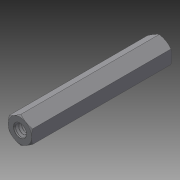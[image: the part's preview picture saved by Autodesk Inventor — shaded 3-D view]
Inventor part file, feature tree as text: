
AUTODESK INVENTOR PART (.ipt)
format: ipt  version: 2015 (Build 190159000, 159)  size: 840,704 bytes
history: native  units: in
note: dims shown in document units (in); Inventor stores cm internally (conversion verified against a paired STEP export)
features: hole x18, sketch x10, other x1, imported_body x1
ambient origin geometry x8: Origin, YZ Plane, XZ Plane, XY Plane, X Axis, Y Axis, Z Axis, Center Point
bodies: Solid1 (feature_tree)
feature tree (30):
  other  "91780A337.sat1"
  hole  "Hole1"  [1 undecoded]
  hole  "Hole2"  [1 undecoded]
  hole  "Hole4"  [1 undecoded]
  hole  "Hole6"  [1 undecoded]
  hole  "Hole8"  [1 undecoded]
  hole  "Hole10"  [1 undecoded]
  hole  "Hole12"  [1 undecoded]
  hole  "Hole14"  [1 undecoded]
  hole  "Hole16"  [1 undecoded]
  hole  "Hole18"  [1 undecoded]
  imported_body  "Base1"
  sketch  "Sketch1"  dims[d0=0.142in d1=0.75in d2=0.375in d3=0.25in d4=0.5635in d5=0.001in d6=0.8108in]
  sketch  "Sketch2"  dims[d7=0.142in d8=0.75in d9=0.375in d10=0.25in d11=0.5635in d12=0.001in d13=0.8108in]
  sketch  "Sketch3"  dims[d14=0.104in d15=0.319in d16=0.375in d17=0.25in d18=0.5635in d19=0.388in d20=120.0deg]
  hole  "Hole3"  [1 undecoded]
  sketch  "Sketch4"  dims[d21=0.104in d22=0.319in d23=0.375in d24=0.25in d25=0.5635in d26=0.388in d27=120.0deg]
  hole  "Hole5"  [1 undecoded]
  sketch  "Sketch5"  dims[d28=0.104in d29=0.319in d30=0.375in d31=0.25in d32=0.5635in d33=0.388in d34=120.0deg]
  hole  "Hole7"  [1 undecoded]
  sketch  "Sketch6"  dims[d35=0.104in d36=0.319in d37=0.375in d38=0.25in d39=0.5635in d40=0.388in d41=120.0deg]
  hole  "Hole9"  [1 undecoded]
  sketch  "Sketch7"  dims[d42=0.104in d43=0.3268in d44=0.375in d45=0.25in d46=0.5635in d47=0.3958in d48=120.0deg]
  hole  "Hole11"  [1 undecoded]
  sketch  "Sketch8"  dims[d49=0.104in d50=0.3268in d51=0.375in d52=0.25in d53=0.5635in d54=0.3958in d55=120.0deg]
  hole  "Hole13"  [1 undecoded]
  sketch  "Sketch9"  dims[d56=0.104in d57=0.3268in d58=0.375in d59=0.25in d60=0.5635in d61=0.3958in d62=120.0deg]
  hole  "Hole15"  [1 undecoded]
  sketch  "Sketch10"  dims[d63=0.104in d64=0.3268in d65=0.375in d66=0.25in d67=0.5635in d68=0.3958in d69=120.0deg]
  hole  "Hole17"  [1 undecoded]
note: 18 required parameter values undecoded (feature->parameter linkage not recoverable at this tier; creation-order binding heuristic only, values carry confidence <= 0.55)
